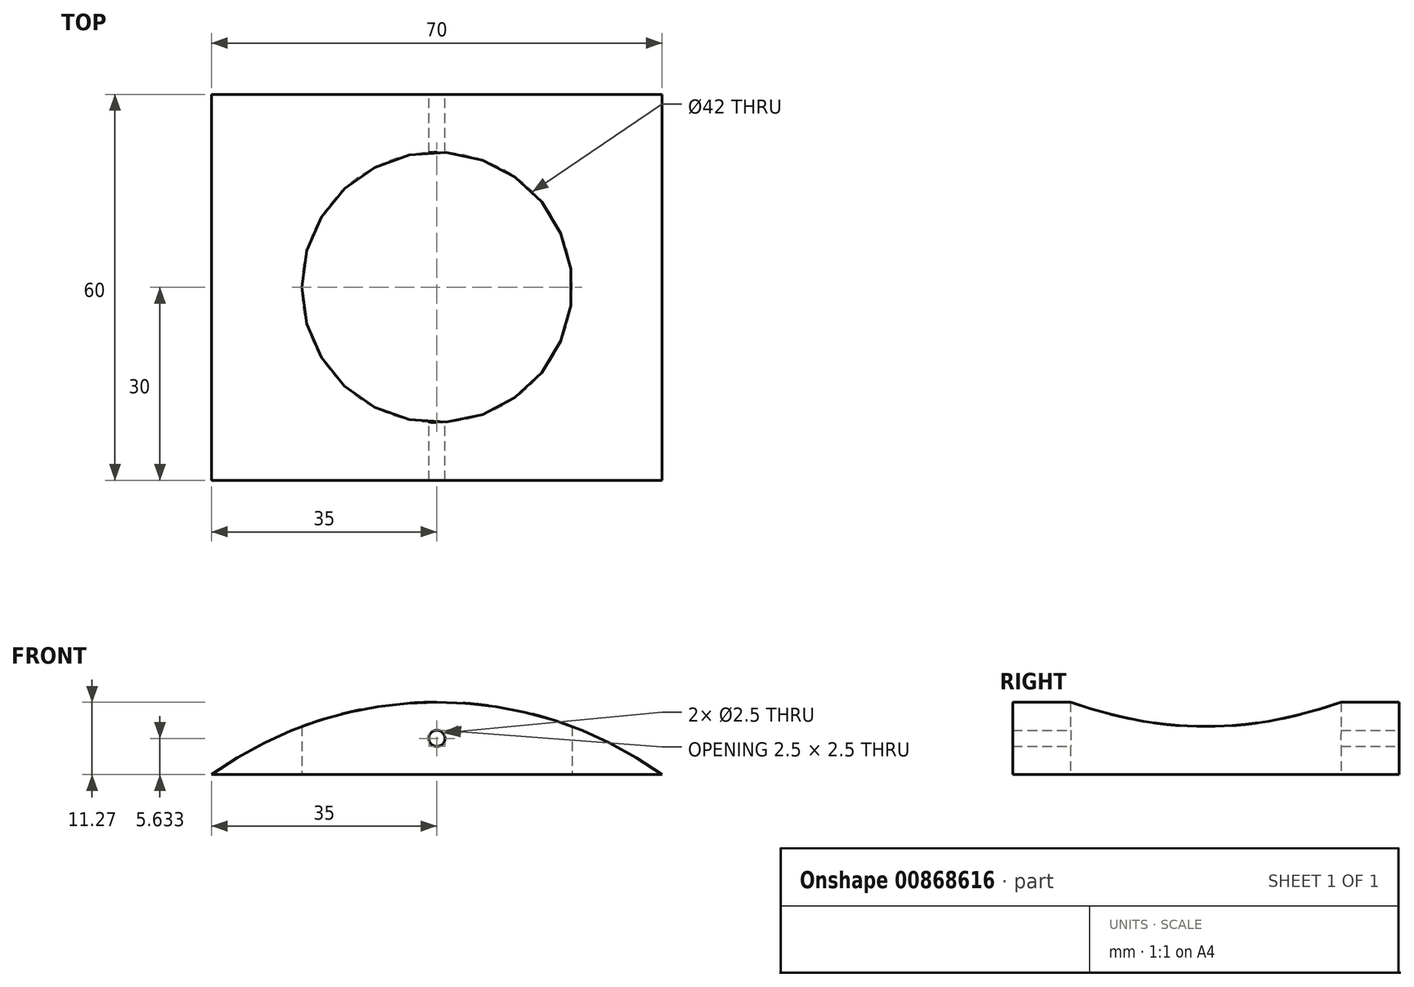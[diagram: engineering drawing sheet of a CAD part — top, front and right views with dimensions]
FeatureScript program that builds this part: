
annotation { "Feature Type Name" : "Feature", "Feature Type Description" : "" }
export const myFeature = defineFeature(function(context is Context, id is Id, definition is map)
    precondition{}
    {
        {
            var Q0;
            Q0=qCreatedBy(makeId("Front.planeOp"),FACE);
            var sketch = newSketch(context, id + "F0", { "sketchPlane" : qUnion([Q0])});
            skCircle(sketch, "E0", {"center": v(0, -48.73) * mm, "radius": 60 * mm});
            skLineSegment(sketch, "E1", {"start": v(-35, 0) * mm, "end": v(35, 0) * mm});
            skCircle(sketch, "E2", {"center": v(0, 5.63) * mm, "radius": 1.25 * mm});
            skLineSegment(sketch, "E3", {"start": v(0, 11.27) * mm, "end": v(0, 0) * mm});
            skSolve(sketch);
        }
        {
            var Q0;
            {var subQ0=sQuery(id+"F0.wireOp",EDGE,"E1");Q0=makeQuery(id+"F0.imprint","IMPRINT",FACE,{"disambiguationData":[TD([[makeQuery(id+"F0.imprint","IMPRINT",EDGE,{"derivedFrom":subQ0}),1.0]])]});}
            extrude(context, id + "F1", {"entities" : qUnion([Q0]), "depth" : 60 * mm, "offsetDistance" : 25 * mm});
        }
        {
            var Q0;
            Q0=makeQuery(id+"F1.opExtrude","SWEPT_FACE",FACE,{"disambiguationData":[OSD([sQuery(id+"F0.wireOp",EDGE,"E1")])]});
            var sketch = newSketch(context, id + "F2", { "sketchPlane" : qUnion([Q0])});
            skPoint(sketch, "E4", {"position": v(-35, 30) * mm});
            skPoint(sketch, "E5", {"position": v(0, 30) * mm});
            skCircle(sketch, "E6", {"center": v(0, 30) * mm, "radius": 21 * mm});
            skSolve(sketch);
        }
        {
            var Q0;
            Q0=makeQuery(id+"F2.imprint","IMPRINT",FACE,{"disambiguationData":[TD([[makeQuery(id+"F2.imprint","IMPRINT",EDGE,{"derivedFrom":sQuery(id+"F2.wireOp",EDGE,"E6")}),1.0]])]});
            extrude(context, id + "F3", {"entities" : qUnion([Q0]), "operationType" : NewBodyOperationType.REMOVE, "oppositeDirection" : true, "depth" : 25 * mm, "offsetDistance" : 25 * mm});
        }
    });
